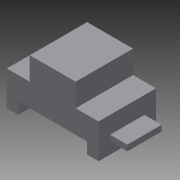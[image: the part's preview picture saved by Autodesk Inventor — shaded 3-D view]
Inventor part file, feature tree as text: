
AUTODESK INVENTOR PART (.ipt)
format: ipt  version: 2015 (Build 190159000, 159)  size: 93,696 bytes
history: native  units: in
note: dims shown in document units (in); Inventor stores cm internally (conversion verified against a paired STEP export)
features: extrude x2, sketch x2
ambient origin geometry x8: Origin, YZ Plane, XZ Plane, XY Plane, X Axis, Y Axis, Z Axis, Center Point
bodies: Solid1 (feature_tree)
feature tree (4):
  extrude  "Extrusion1"  Depth=1.0in
  extrude  "Extrusion2"  Depth=3.0in
  sketch  "Sketch1"  dims[d0=1.5in d1=1.0in]
  sketch  "Sketch2"  dims[d2=2.0in d3=3.0in d4=0.5in d5=0.5in d6=0.5in d7=0.5in d8=1.0in d9=2.5in d10=0.0in d11=0.75in d12=0.0in d13=1.5in d14=0.25in]
